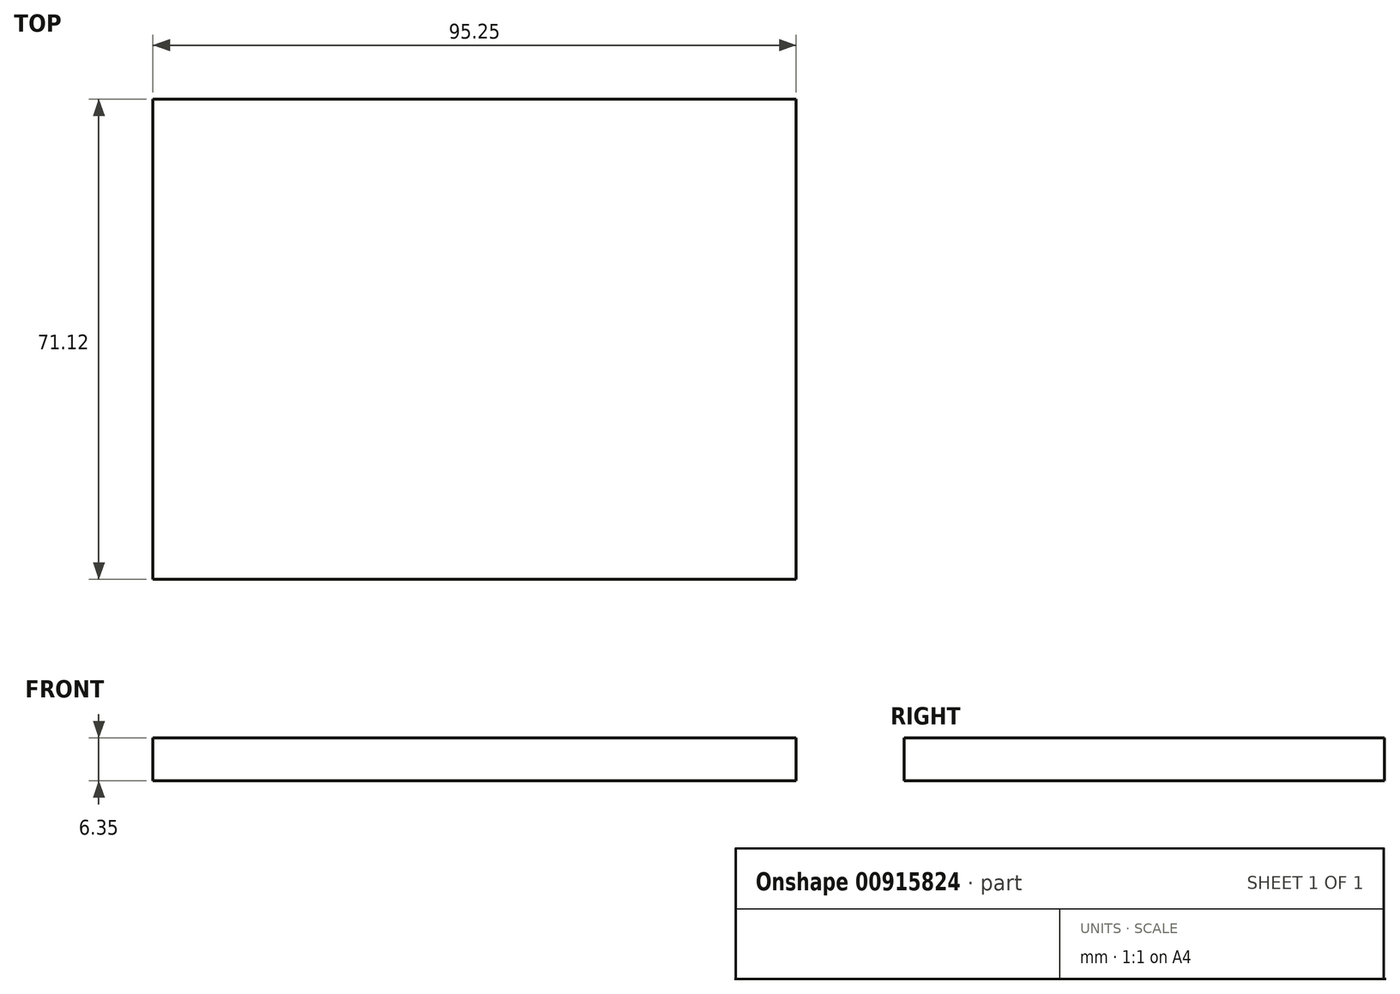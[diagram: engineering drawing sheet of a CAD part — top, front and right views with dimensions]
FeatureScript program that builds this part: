
annotation { "Feature Type Name" : "Feature", "Feature Type Description" : "" }
export const myFeature = defineFeature(function(context is Context, id is Id, definition is map)
    precondition{}
    {
        {
            var Q0;
            Q0=qCreatedBy(makeId("Top.planeOp"),FACE);
            var sketch = newSketch(context, id + "F0", { "sketchPlane" : qUnion([Q0])});
            skLineSegment(sketch, "E0.bottom", {"start": v(0, 0) * mm, "end": v(95.25, 0) * mm});
            skLineSegment(sketch, "E0.top", {"start": v(0, -71.12) * mm, "end": v(95.25, -71.12) * mm});
            skLineSegment(sketch, "E0.left", {"start": v(0, 0) * mm, "end": v(0, -71.12) * mm});
            skLineSegment(sketch, "E0.right", {"start": v(95.25, 0) * mm, "end": v(95.25, -71.12) * mm});
            skSolve(sketch);
        }
        {
            var Q0;
            Q0=makeQuery(id+"F0.imprint","IMPRINT",FACE,{"disambiguationData":[TD([[makeQuery(id+"F0.imprint","IMPRINT",EDGE,{"derivedFrom":sQuery(id+"F0.wireOp",EDGE,"E0.bottom")}),-1.0]])]});
            extrude(context, id + "F1", {"entities" : qUnion([Q0]), "depth" : 6.35 * mm, "offsetDistance" : 25.4 * mm});
        }
    });
